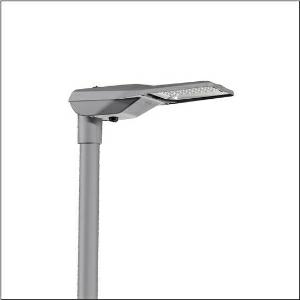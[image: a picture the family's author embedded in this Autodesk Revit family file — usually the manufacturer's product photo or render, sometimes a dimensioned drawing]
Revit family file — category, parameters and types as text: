
# Revit family: streetlight_sl_21_mini___st0_8a_5xe2c63t08hb_8657
name_source: partatom
category: Lighting Fixtures
units: mm (PartAtom-declared; Revit-internal decimal feet)

## family parameters
Cut with Voids When Loaded = No
Host = Face
Light Source = No
Part Type = Normal
Room Calculation Point = No
Round Connector Dimension = Use Diameter
Shared = No

## types (1)
- --- (1 x LED, 8110 lm, 66 W, 2700K)
    Apparent Load = 66 VA
    CIE Flux Codes = 38 75 97 100 100
    Color Rendering = 70
    Color Temperature = 2700K
    Default Elevation = 1800 mm
    Description = Streetlight SL 21 mini, mast luminaire, primary light control with lens, of PMMA, primary optical cover: cover, of toughened safety glass, transparent, light distribution: ST0.8a, light emission: direct distribution, primary light characteristic: asymmetric, installation type: side-entry, post-top, LED, High Power LED, rated luminous flux: 8.110lm, luminous efficacy: 123lm/W, light colour: 727, colour temperature: 2700K, control gear: D4i, control: overheat protection, constant luminous flux control, time-dependent luminous flux control, flexible luminous flux parameterisation, pre-setting: logarithmic dimming characteristic, mains connection: 220..240V, AC, 50/60Hz, start of lifetime: 66W, end of service life: 69W, reduction: 30W, luminaire housing, of diecast aluminium, powder-coated, SITECO metallic grey (DB 702S), corrosivity category C5 high according to DIN EN ISO 12944, please order mast flange separately, inclination adjustable: 0°, 5°, 10°, 15°, sealing non-destructively replaceable, multi-level sealing system, length: 628mm, width: 235mm, height: 110mm, mast flange for spigot size: 42mm (side-entry): 5XC10008XM4, 60/48mm (side-entry/post-top): 5XC10108XM2, 76/60mm (side-entry/post-top): 5XC10108XM1, mounting height: 4..8m, Smart Interface below and above, protection rating (complete): IP66, insulation class (complete): insulation class II (safety insulation), certification: CE, ENEC, ENEC+, VDE, impact resistance: IK10, permissible operating ambient temperature for outdoor applications: -40..+50°C, standard-compliant lighting for roads and squares, packaging unit: 1 piece

Light Distribution: ST0.8a
    Height = 110 mm
    Lamp = 1 x LED
    Lamp Light Flux = 8110 lm
    Lamp Power = 66 W
    Lamp count = 1
    Length = 625 mm
    Luminous efficacy = 123 lm/W
    Manufacturer = Siteco
    ModVariant = No
    Model = 5XE2C63T08HB
    Number of Poles = 1
    OnlyDefault = Yes
    Power Factor = 1
    Product Name = Streetlight SL 21 mini | ST0.8a
    Product group = mast luminaire | pylon top
    ProductGroupID = 6100
    Protection Class = Protection class II
    Protection Degree = IP 66
    RLX_Detail_Level = 1
    RLX_Emergency_Light_Flux = 0 lm
    RLX_Emergency_Type = 0
    RLX_Emergency_Type_DB = No
    RlxData = <blob elided: 26293 chars, md5=3c94ba58>
    Socket = socket
    Standby Power = 0 W
    System Light Flux = 8110 lm
    System Power = 66 W
    Type Comments = factory setting: luminous flux: 100 % | dim-lin: 254 | 670 mA
    Type Image = l_1003514.jpg
    URL = http://relux.com
    VarID = @adj_182699
    Voltage = 0 V
    Weight = 0.00 kg
    Width = 234 mm

## geometry (parser evidence)
native form markers: Blend x4, Sweep x11
no freeform markers — native parametric forms only
